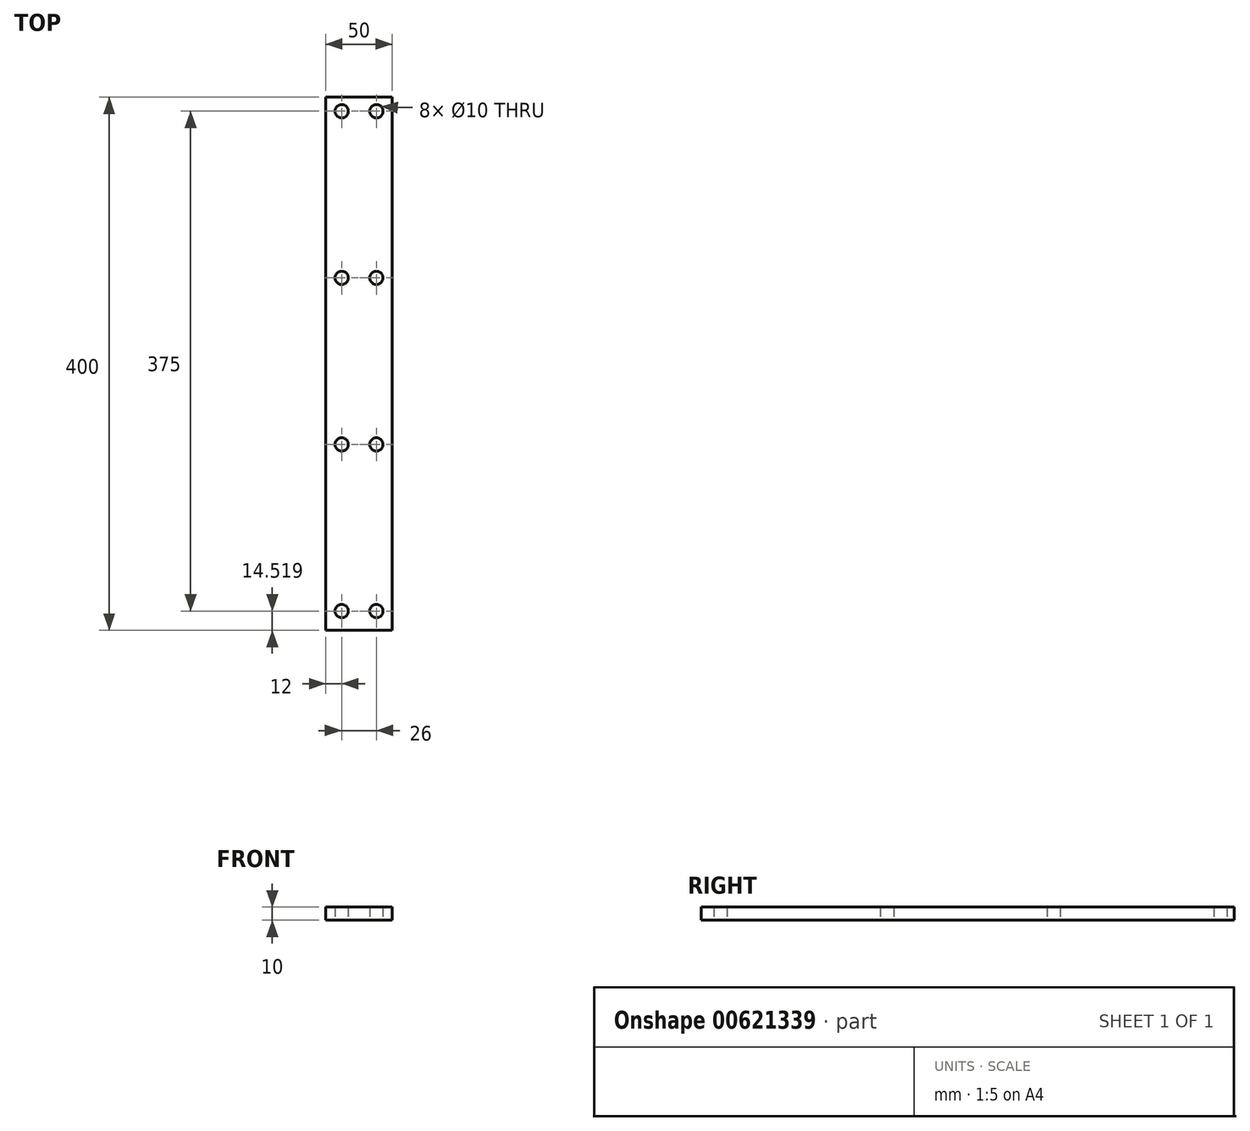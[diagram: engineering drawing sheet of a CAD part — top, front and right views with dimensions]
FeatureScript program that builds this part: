
annotation { "Feature Type Name" : "Feature", "Feature Type Description" : "" }
export const myFeature = defineFeature(function(context is Context, id is Id, definition is map)
    precondition{}
    {
        {
            var Q0;
            Q0=qCreatedBy(makeId("Top.planeOp"),FACE);
            var sketch = newSketch(context, id + "F0", { "sketchPlane" : qUnion([Q0])});
            skLineSegment(sketch, "E0.bottom", {"start": v(0, 0) * mm, "end": v(50, 0) * mm});
            skLineSegment(sketch, "E0.top", {"start": v(0, 400) * mm, "end": v(50, 400) * mm});
            skLineSegment(sketch, "E0.left", {"start": v(0, 0) * mm, "end": v(0, 400) * mm});
            skLineSegment(sketch, "E0.right", {"start": v(50, 0) * mm, "end": v(50, 400) * mm});
            skCircle(sketch, "E1", {"center": v(12, 14.52) * mm, "radius": 5 * mm});
            skCircle(sketch, "E2.0.1.0", {"center": v(12, 139.52) * mm, "radius": 5 * mm});
            skCircle(sketch, "E2.0.2.0", {"center": v(12, 264.52) * mm, "radius": 5 * mm});
            skCircle(sketch, "E2.0.3.0", {"center": v(12, 389.52) * mm, "radius": 5 * mm});
            skCircle(sketch, "E2.1.0.0", {"center": v(38, 14.52) * mm, "radius": 5 * mm});
            skCircle(sketch, "E2.1.1.0", {"center": v(38, 139.52) * mm, "radius": 5 * mm});
            skCircle(sketch, "E2.1.2.0", {"center": v(38, 264.52) * mm, "radius": 5 * mm});
            skCircle(sketch, "E2.1.3.0", {"center": v(38, 389.52) * mm, "radius": 5 * mm});
            skLineSegment(sketch, "E2.direction1", {"start": v(12, 14.52) * mm, "end": v(38, 14.52) * mm, "construction": true});
            skLineSegment(sketch, "E2.direction2", {"start": v(12, 14.52) * mm, "end": v(12, 139.52) * mm, "construction": true});
            skSolve(sketch);
        }
        {
            var Q0;
            Q0 = qSketchRegion(id + "F0", true);
            extrude(context, id + "F1", {"entities" : qUnion([Q0]), "depth" : 10 * mm, "offsetDistance" : 25 * mm});
        }
    });
